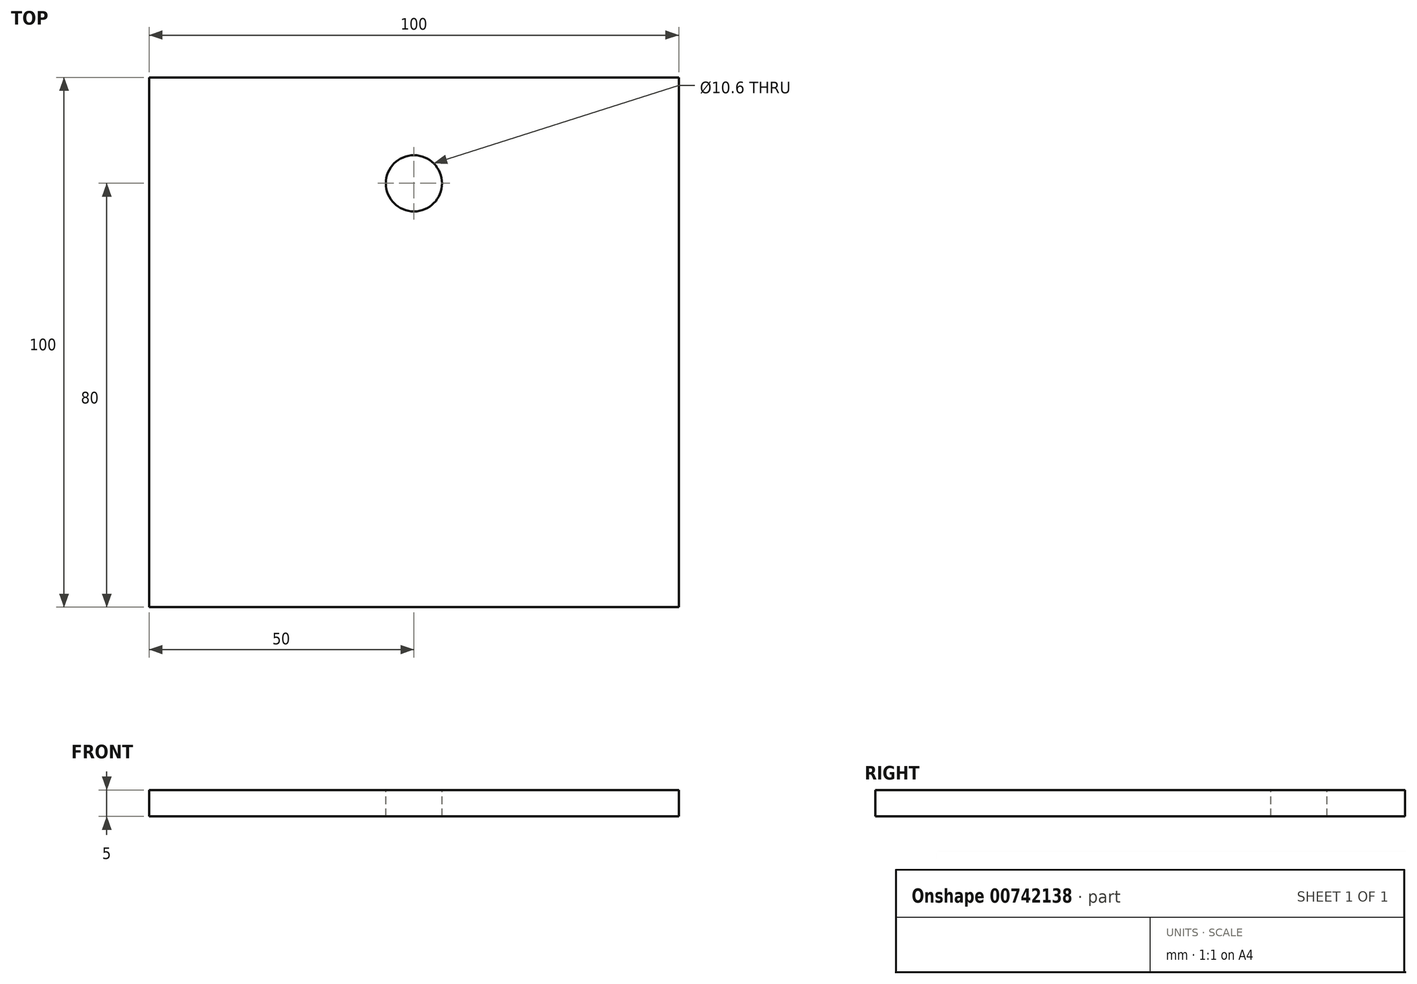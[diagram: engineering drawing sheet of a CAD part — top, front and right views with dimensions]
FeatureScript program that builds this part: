
annotation { "Feature Type Name" : "Feature", "Feature Type Description" : "" }
export const myFeature = defineFeature(function(context is Context, id is Id, definition is map)
    precondition{}
    {
        {
            var Q0;
            Q0=qCreatedBy(makeId("Top.planeOp"),FACE);
            var sketch = newSketch(context, id + "F0", { "sketchPlane" : qUnion([Q0])});
            skLineSegment(sketch, "E0.bottom", {"start": v(0, 0) * mm, "end": v(100, 0) * mm});
            skLineSegment(sketch, "E0.top", {"start": v(0, 100) * mm, "end": v(100, 100) * mm});
            skLineSegment(sketch, "E0.left", {"start": v(0, 0) * mm, "end": v(0, 100) * mm});
            skLineSegment(sketch, "E0.right", {"start": v(100, 0) * mm, "end": v(100, 100) * mm});
            skSolve(sketch);
        }
        {
            var Q0;
            Q0 = qSketchRegion(id + "F0", true);
            extrude(context, id + "F1", {"entities" : qUnion([Q0]), "depth" : 5 * mm, "offsetDistance" : 25 * mm});
        }
        {
            var Q0;
            Q0=makeQuery(id+"F1.opExtrude","CAP_FACE",FACE,{"disambiguationData":[OSD([sQuery(id+"F0.wireOp",EDGE,"E0.bottom"),sQuery(id+"F0.wireOp",EDGE,"E0.top"),sQuery(id+"F0.wireOp",EDGE,"E0.left"),sQuery(id+"F0.wireOp",EDGE,"E0.right")])],"isStart":false});
            var sketch = newSketch(context, id + "F2", { "sketchPlane" : qUnion([Q0])});
            skCircle(sketch, "E1", {"center": v(50, 80) * mm, "radius": 5.3 * mm});
            skLineSegment(sketch, "E2", {"start": v(50, 80) * mm, "end": v(50, 100) * mm});
            skSolve(sketch);
        }
        {
            var Q0;
            Q0=makeQuery(id+"F2.imprint","IMPRINT",FACE,{"disambiguationData":[TD([[makeQuery(id+"F2.imprint","IMPRINT",EDGE,{"derivedFrom":sQuery(id+"F2.wireOp",EDGE,"E1")}),1.0]])]});
            extrude(context, id + "F3", {"entities" : qUnion([Q0]), "operationType" : NewBodyOperationType.REMOVE, "oppositeDirection" : true, "depth" : 25 * mm, "offsetDistance" : 25 * mm});
        }
        {
            var Q0;
            Q0=makeQuery(id+"F1.opExtrude","SWEPT_FACE",FACE,{"disambiguationData":[OSD([sQuery(id+"F0.wireOp",EDGE,"E0.bottom")])]});
            var Q1;
            Q1=makeQuery(id+"F1.opExtrude","SWEPT_FACE",FACE,{"disambiguationData":[OSD([sQuery(id+"F0.wireOp",EDGE,"E0.top")])]});
            cPlane(context, id + "F4", {"entities" : qUnion([Q0, Q1]), "cplaneType" : CPlaneType.MID_PLANE, "offset" : 25 * mm, "width" : 150 * mm, "height" : 150 * mm});
        }
        {
            var Q0;
            Q0=qCreatedBy(id+"F4.planeOp",FACE);
            var sketch = newSketch(context, id + "F5", { "sketchPlane" : qUnion([Q0])});
            skLineSegment(sketch, "E3.0", {"start": v(0, 5) * mm, "end": v(100, 5) * mm});
            skLineSegment(sketch, "E4.0", {"start": v(0, 0) * mm, "end": v(100, 0) * mm});
            skLineSegment(sketch, "E5", {"start": v(50, 5) * mm, "end": v(50, 0) * mm});
            skSolve(sketch);
        }
    });
